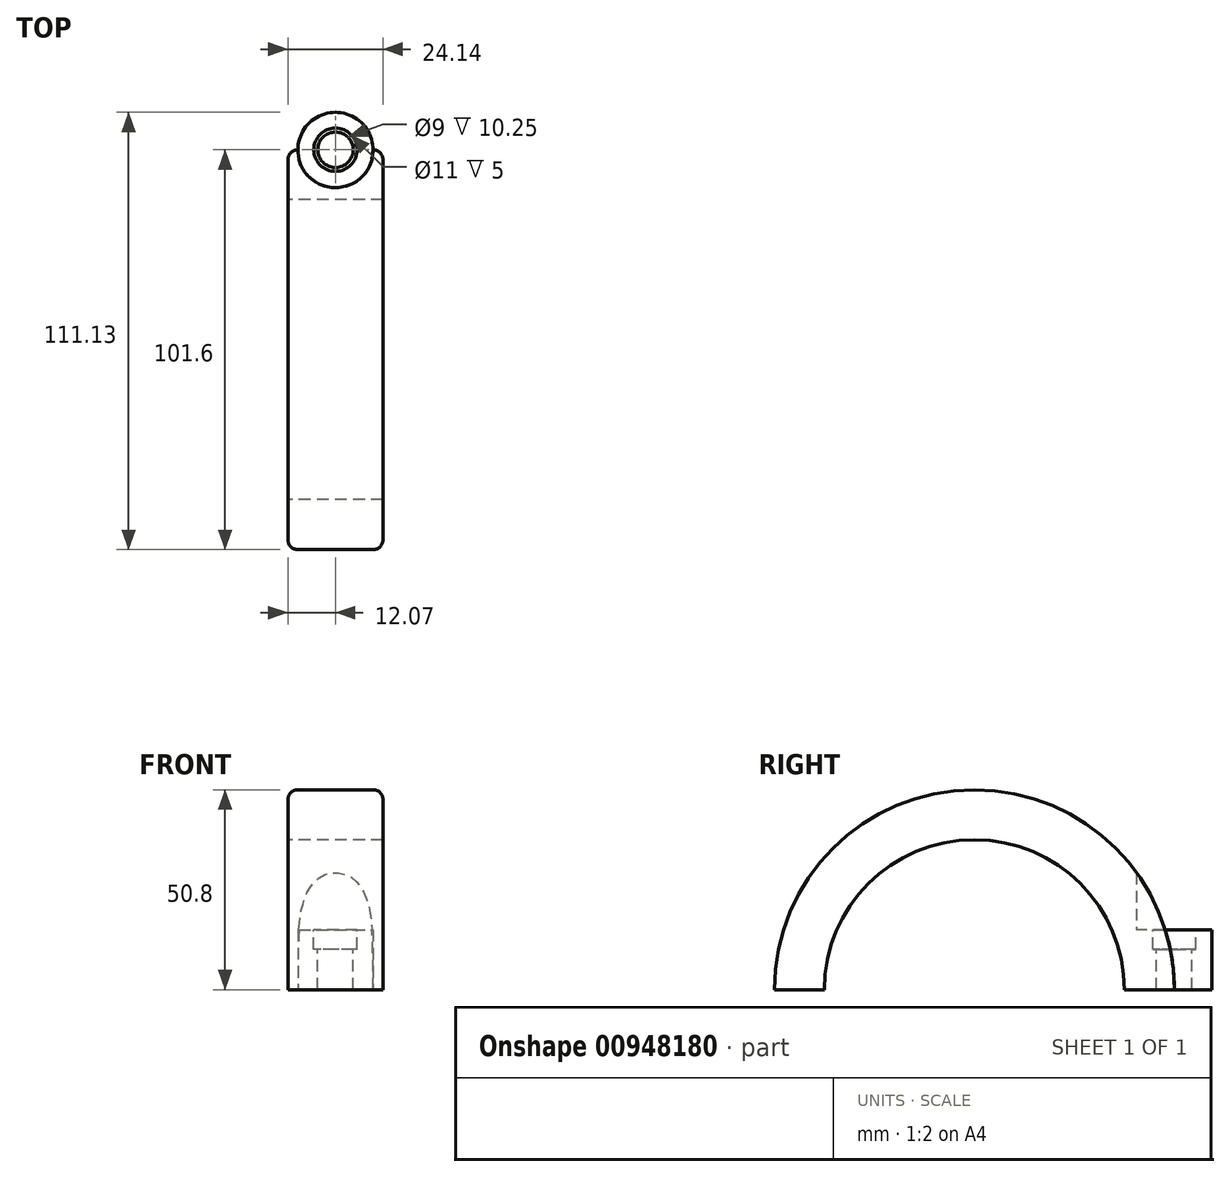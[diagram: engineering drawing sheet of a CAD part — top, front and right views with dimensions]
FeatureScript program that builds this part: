
annotation { "Feature Type Name" : "Feature", "Feature Type Description" : "" }
export const myFeature = defineFeature(function(context is Context, id is Id, definition is map)
    precondition{}
    {
        {
            var Q0;
            Q0=qCreatedBy(makeId("Right.planeOp"),FACE);
            var sketch = newSketch(context, id + "F0", { "sketchPlane" : qUnion([Q0])});
            skArc(sketch, "E0", {"start": v(38.1, 0) * mm, "mid": v(0, 38.1) * mm, "end": v(-38.1, 0) * mm});
            skArc(sketch, "E1.0", {"start": v(50.8, 0) * mm, "mid": v(0, 50.8) * mm, "end": v(-50.8, 0) * mm});
            skLineSegment(sketch, "E2", {"start": v(-50.8, 0) * mm, "end": v(-38.1, 0) * mm});
            skLineSegment(sketch, "E3.trimOffspring", {"start": v(38.1, 0) * mm, "end": v(50.8, 0) * mm});
            skPoint(sketch, "E4.orphan", {"position": v(-78.76, 0) * mm});
            skSolve(sketch);
        }
        {
            var Q0;
            Q0 = qSketchRegion(id + "F0", true);
            extrude(context, id + "F1", {"entities" : qUnion([Q0]), "endBound" : BoundingType.SYMMETRIC, "depth" : 24.13 * mm, "offsetDistance" : 25 * mm});
        }
        {
            var Q0;
            Q0=makeQuery(id+"F1.opExtrude","SWEPT_FACE",FACE,{"disambiguationData":[OSD([sQuery(id+"F0.wireOp",EDGE,"E3.trimOffspring")])]});
            var sketch = newSketch(context, id + "F2", { "sketchPlane" : qUnion([Q0])});
            skPoint(sketch, "E5", {"position": v(0, -50.8) * mm});
            skCircle(sketch, "E6", {"center": v(0, -50.8) * mm, "radius": 9.53 * mm});
            skSolve(sketch);
        }
        {
            var Q0;
            Q0 = qSketchRegion(id + "F2", true);
            extrude(context, id + "F3", {"entities" : qUnion([Q0]), "operationType" : NewBodyOperationType.ADD, "oppositeDirection" : true, "depth" : 15.25 * mm, "offsetDistance" : 25 * mm});
        }
        {
            var Q0;
            Q0=makeQuery(id+"F3.opExtrude","CAP_FACE",FACE,{"disambiguationData":[OSD([sQuery(id+"F2.wireOp",EDGE,"E6")])],"isStart":false});
            var sketch = newSketch(context, id + "F4", { "sketchPlane" : qUnion([Q0])});
            skPoint(sketch, "E7", {"position": v(0, 50.8) * mm});
            skCircle(sketch, "E8", {"center": v(0, 50.8) * mm, "radius": 9.62 * mm});
            skSolve(sketch);
        }
        {
            var Q0;
            Q0 = qSketchRegion(id + "F4", true);
            extrude(context, id + "F5", {"entities" : qUnion([Q0]), "operationType" : NewBodyOperationType.REMOVE, "depth" : 25 * mm, "offsetDistance" : 25 * mm});
        }
        {
            var Q0;
            Q0=makeQuery(id+"F5.boolean.opBoolean","MERGE",FACE,{"derivedFrom":[makeQuery(id+"F3.opExtrude","CAP_FACE",FACE,{"disambiguationData":[OSD([sQuery(id+"F2.wireOp",EDGE,"E6")])],"isStart":false})],"fromTools":[makeQuery(id+"F5.opExtrude","CAP_FACE",FACE,{"disambiguationData":[OSD([sQuery(id+"F4.wireOp",EDGE,"E8")])],"isStart":true})]});
            var sketch = newSketch(context, id + "F6", { "sketchPlane" : qUnion([Q0])});
            skCircle(sketch, "E9", {"center": v(0, 50.8) * mm, "radius": 4.53 * mm});
            skSolve(sketch);
        }
        {
            var Q0;
            Q0=sQuery(id+"F6.wireOp",VERTEX,"E9.center");
            var Q1;
            Q1=makeQuery(id+"F1.opExtrude","SWEPT_BODY",BODY,{"disambiguationData":[OSD([sQuery(id+"F0.wireOp",EDGE,"E0"),sQuery(id+"F0.wireOp",EDGE,"E1.0"),sQuery(id+"F0.wireOp",EDGE,"E2"),sQuery(id+"F0.wireOp",EDGE,"E3.trimOffspring")])]});
            hole(context, id + "F7", {"style" : HoleStyle.C_BORE, "endStyle" : HoleEndStyle.BLIND, "holeDiameter" : 9 * mm, "cBoreDiameter" : 11 * mm, "cBoreDepth" : 5 * mm, "majorDiameter" : 5 * mm, "holeDepth" : 75 * mm, "isTappedThrough" : true, "tappedDepth" : 12 * mm, "tapClearance" : 3, "startFromSketch" : true, "locations" : qUnion([Q0]), "scope" : qUnion([Q1])});
        }
        {
            var Q0;
            Q0=makeQuery(id+"F1.opExtrude","CAP_EDGE",EDGE,{"disambiguationData":[OSD([sQuery(id+"F0.wireOp",EDGE,"E1.0")])],"isStart":false});
            var Q1;
            Q1=makeQuery(id+"F1.opExtrude","CAP_EDGE",EDGE,{"disambiguationData":[OSD([sQuery(id+"F0.wireOp",EDGE,"E1.0")])],"isStart":true});
            fillet(context, id + "F8", {"entities" : qUnion([Q0, Q1]), "radius" : 2.5 * mm, "tangentPropagation" : true, "allowEdgeOverflow" : false});
        }
    });
